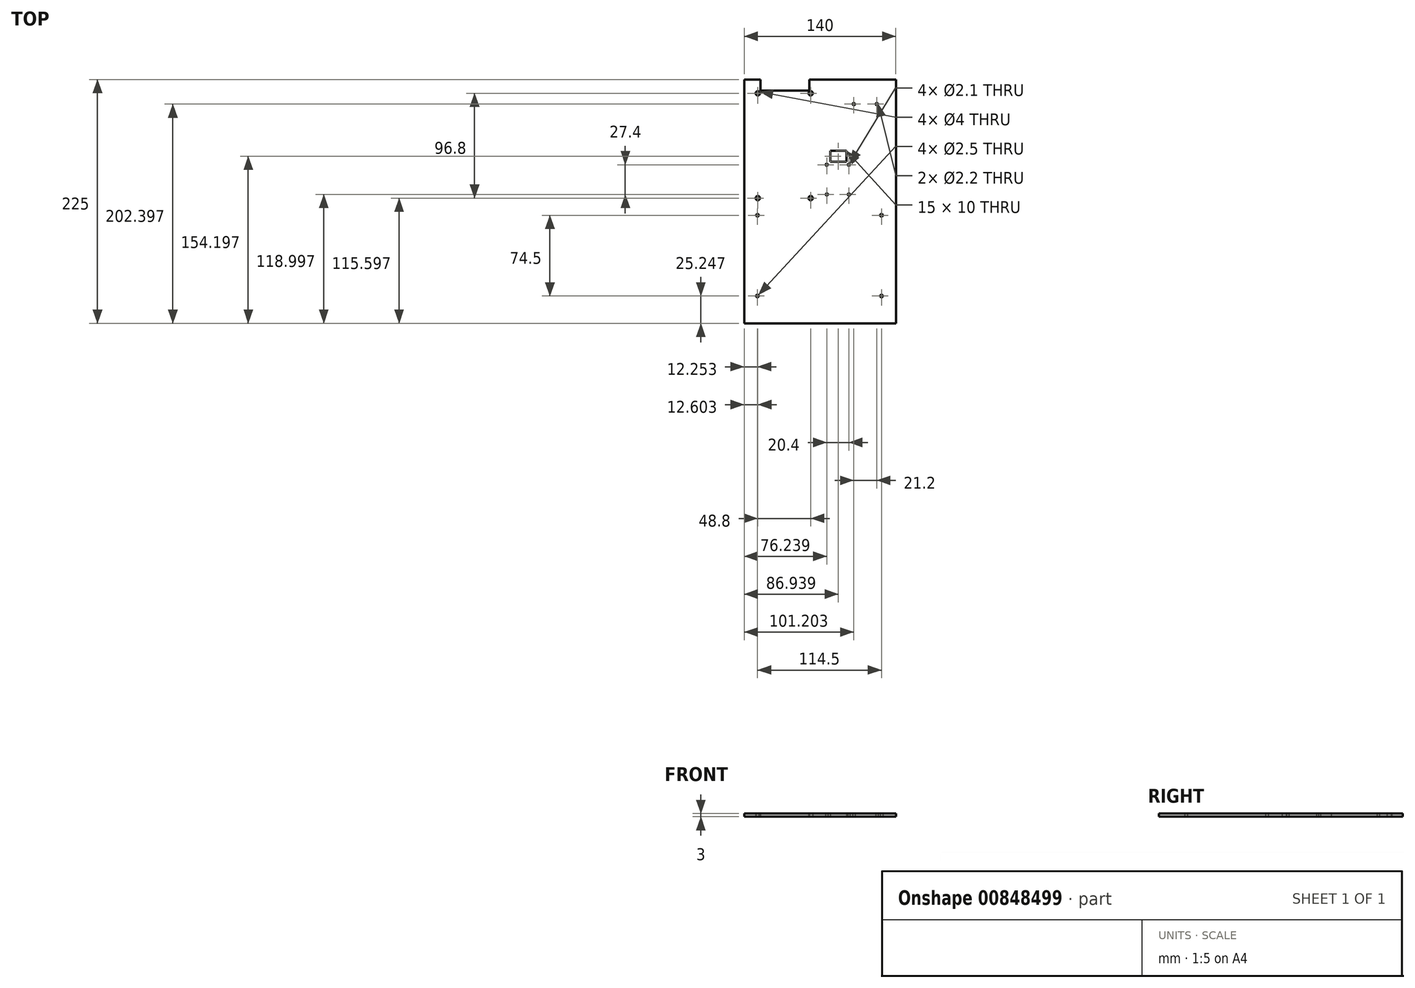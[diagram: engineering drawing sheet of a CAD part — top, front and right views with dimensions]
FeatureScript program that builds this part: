
annotation { "Feature Type Name" : "Feature", "Feature Type Description" : "" }
export const myFeature = defineFeature(function(context is Context, id is Id, definition is map)
    precondition{}
    {
        {
            var Q0;
            Q0=qCreatedBy(makeId("Top.planeOp"),FACE);
            var sketch = newSketch(context, id + "F0", { "sketchPlane" : qUnion([Q0])});
            skLineSegment(sketch, "E0.bottom", {"start": v(-96.6, 98.7) * mm, "end": v(43.4, 98.7) * mm});
            skLineSegment(sketch, "E0.top", {"start": v(-96.6, -126.3) * mm, "end": v(43.4, -126.3) * mm});
            skLineSegment(sketch, "E0.left", {"start": v(-96.6, 98.7) * mm, "end": v(-96.6, -126.3) * mm});
            skLineSegment(sketch, "E0.right", {"start": v(43.4, 98.7) * mm, "end": v(43.4, -126.3) * mm});
            skLineSegment(sketch, "E1.bottom", {"start": v(-86.6, 88.7) * mm, "end": v(-32.6, 88.7) * mm});
            skLineSegment(sketch, "E1.top", {"start": v(-86.6, -13.3) * mm, "end": v(-32.6, -13.3) * mm});
            skLineSegment(sketch, "E1.left", {"start": v(-86.6, 88.7) * mm, "end": v(-86.6, -13.3) * mm});
            skLineSegment(sketch, "E1.right", {"start": v(-32.6, 88.7) * mm, "end": v(-32.6, -13.3) * mm});
            skLineSegment(sketch, "E2.bottom", {"start": v(-87.6, -23.3) * mm, "end": v(33.4, -23.3) * mm});
            skLineSegment(sketch, "E2.top", {"start": v(-87.6, -104.3) * mm, "end": v(33.4, -104.3) * mm});
            skLineSegment(sketch, "E2.left", {"start": v(-87.6, -23.3) * mm, "end": v(-87.6, -104.3) * mm});
            skLineSegment(sketch, "E2.right", {"start": v(33.4, -23.3) * mm, "end": v(33.4, -104.3) * mm});
            skLineSegment(sketch, "E3.bottom", {"start": v(-23.16, 22.9) * mm, "end": v(2.84, 22.9) * mm});
            skLineSegment(sketch, "E3.top", {"start": v(-23.16, -10.1) * mm, "end": v(2.84, -10.1) * mm});
            skLineSegment(sketch, "E3.left", {"start": v(-23.16, 22.9) * mm, "end": v(-23.16, -10.1) * mm});
            skLineSegment(sketch, "E3.right", {"start": v(2.84, 22.9) * mm, "end": v(2.84, -10.1) * mm});
            skLineSegment(sketch, "E4.bottom", {"start": v(2, 78.7) * mm, "end": v(28.4, 78.7) * mm});
            skLineSegment(sketch, "E4.top", {"start": v(2, 42.9) * mm, "end": v(28.4, 42.9) * mm});
            skLineSegment(sketch, "E4.left", {"start": v(2, 78.7) * mm, "end": v(2, 42.9) * mm});
            skLineSegment(sketch, "E4.right", {"start": v(28.4, 78.7) * mm, "end": v(28.4, 42.9) * mm});
            skLineSegment(sketch, "E5", {"start": v(2.84, 22.9) * mm, "end": v(-2.16, 22.9) * mm});
            skLineSegment(sketch, "E6", {"start": v(-2.16, 22.9) * mm, "end": v(-17.16, 22.9) * mm});
            skLineSegment(sketch, "E7", {"start": v(-2.16, 22.9) * mm, "end": v(-2.16, 32.9) * mm});
            skLineSegment(sketch, "E8.bottom", {"start": v(-17.16, 22.9) * mm, "end": v(-2.16, 22.9) * mm});
            skLineSegment(sketch, "E8.top", {"start": v(-17.16, 32.9) * mm, "end": v(-2.16, 32.9) * mm});
            skLineSegment(sketch, "E8.left", {"start": v(-17.16, 22.9) * mm, "end": v(-17.16, 32.9) * mm});
            skLineSegment(sketch, "E9.bottom", {"start": v(-81.6, 98.7) * mm, "end": v(-36.6, 98.7) * mm});
            skLineSegment(sketch, "E9.top", {"start": v(-81.6, 88.7) * mm, "end": v(-36.6, 88.7) * mm});
            skLineSegment(sketch, "E9.left", {"start": v(-81.6, 98.7) * mm, "end": v(-81.6, 88.7) * mm});
            skLineSegment(sketch, "E9.right", {"start": v(-36.6, 98.7) * mm, "end": v(-36.6, 88.7) * mm});
            skLineSegment(sketch, "E10", {"start": v(33.4, -23.3) * mm, "end": v(33.4, -43.3) * mm});
            skLineSegment(sketch, "E11.bottom", {"start": v(33.4, -43.3) * mm, "end": v(43.4, -43.3) * mm});
            skLineSegment(sketch, "E11.top", {"start": v(33.4, -23.3) * mm, "end": v(43.4, -23.3) * mm});
            skLineSegment(sketch, "E11.left", {"start": v(33.4, -43.3) * mm, "end": v(33.4, -23.3) * mm});
            skLineSegment(sketch, "E11.right", {"start": v(43.4, -43.3) * mm, "end": v(43.4, -23.3) * mm});
            skCircle(sketch, "E12", {"center": v(-84.35, -101.04) * mm, "radius": 1.25 * mm});
            skCircle(sketch, "E13", {"center": v(-84.35, -26.54) * mm, "radius": 1.25 * mm});
            skCircle(sketch, "E14", {"center": v(30.15, -26.54) * mm, "radius": 1.25 * mm});
            skCircle(sketch, "E15", {"center": v(30.15, -101.04) * mm, "radius": 1.25 * mm});
            skCircle(sketch, "E16", {"center": v(4.6, 76.1) * mm, "radius": 1.1 * mm});
            skCircle(sketch, "E17", {"center": v(25.8, 76.1) * mm, "radius": 1.1 * mm});
            skCircle(sketch, "E18", {"center": v(0.04, 20.1) * mm, "radius": 1.05 * mm});
            skCircle(sketch, "E19", {"center": v(0.04, -7.3) * mm, "radius": 1.05 * mm});
            skCircle(sketch, "E20", {"center": v(-20.36, -7.3) * mm, "radius": 1.05 * mm});
            skCircle(sketch, "E21", {"center": v(-20.36, 20.1) * mm, "radius": 1.05 * mm});
            skLineSegment(sketch, "E22.bottom", {"start": v(-86.6, 88.7) * mm, "end": v(-84.4, 88.7) * mm});
            skLineSegment(sketch, "E22.left", {"start": v(-86.6, 88.7) * mm, "end": v(-86.6, 86.5) * mm});
            skLineSegment(sketch, "E23.bottom", {"start": v(-86.6, 88.7) * mm, "end": v(-84, 88.7) * mm});
            skLineSegment(sketch, "E23.left", {"start": v(-86.6, 88.7) * mm, "end": v(-86.6, 86.1) * mm});
            skCircle(sketch, "E24", {"center": v(-84, 86.1) * mm, "radius": 2 * mm});
            skLineSegment(sketch, "E25.bottom", {"start": v(-32.6, 88.7) * mm, "end": v(-35.2, 88.7) * mm});
            skLineSegment(sketch, "E25.left", {"start": v(-32.6, 88.7) * mm, "end": v(-32.6, 86.1) * mm});
            skCircle(sketch, "E26", {"center": v(-35.2, 86.1) * mm, "radius": 2 * mm});
            skLineSegment(sketch, "E27.bottom", {"start": v(-32.6, -13.3) * mm, "end": v(-35.2, -13.3) * mm});
            skLineSegment(sketch, "E27.left", {"start": v(-32.6, -13.3) * mm, "end": v(-32.6, -10.7) * mm});
            skLineSegment(sketch, "E28.bottom", {"start": v(-86.6, -13.3) * mm, "end": v(-84, -13.3) * mm});
            skLineSegment(sketch, "E28.left", {"start": v(-86.6, -13.3) * mm, "end": v(-86.6, -10.7) * mm});
            skCircle(sketch, "E29", {"center": v(-84, -10.7) * mm, "radius": 2 * mm});
            skCircle(sketch, "E30", {"center": v(-35.2, -10.7) * mm, "radius": 2 * mm});
            skSolve(sketch);
        }
        {
            var Q0;
            Q0=makeQuery(id+"F0.imprint","IMPRINT",FACE,{"disambiguationData":[TD([[makeQuery(id+"F0.imprint","IMPRINT",EDGE,{"derivedFrom":sQuery(id+"F0.wireOp",EDGE,"E2.bottom")}),-1.0]])]});
            var Q1;
            {var subQ1=sQuery(id+"F0.wireOp",EDGE,"E0.top");Q1=makeQuery(id+"F0.imprint","IMPRINT",FACE,{"disambiguationData":[TD([[makeQuery(id+"F0.imprint","IMPRINT",EDGE,{"derivedFrom":subQ1}),1.0]])]});}
            var Q2;
            Q2=makeQuery(id+"F0.imprint","IMPRINT",FACE,{"disambiguationData":[TD([[makeQuery(id+"F0.imprint","IMPRINT",EDGE,{"derivedFrom":sQuery(id+"F0.wireOp",EDGE,"E1.top")}),1.0]])]});
            var Q3;
            Q3=makeQuery(id+"F0.imprint","IMPRINT",FACE,{"disambiguationData":[TD([[makeQuery(id+"F0.imprint","IMPRINT",EDGE,{"derivedFrom":sQuery(id+"F0.wireOp",EDGE,"E3.bottom")}),-1.0]])]});
            var Q4;
            Q4=makeQuery(id+"F0.imprint","IMPRINT",FACE,{"disambiguationData":[TD([[makeQuery(id+"F0.imprint","IMPRINT",EDGE,{"derivedFrom":sQuery(id+"F0.wireOp",EDGE,"E8.bottom")}),1.0]])]});
            var Q5;
            Q5=makeQuery(id+"F0.imprint","IMPRINT",FACE,{"disambiguationData":[TD([[makeQuery(id+"F0.imprint","IMPRINT",EDGE,{"derivedFrom":sQuery(id+"F0.wireOp",EDGE,"E4.bottom")}),-1.0]])]});
            var Q6;
            Q6=makeQuery(id+"F0.imprint","IMPRINT",FACE,{"disambiguationData":[TD([[makeQuery(id+"F0.imprint","IMPRINT",EDGE,{"derivedFrom":sQuery(id+"F0.wireOp",EDGE,"E11.bottom")}),1.0]])]});
            var Q7;
            Q7=makeQuery(id+"F0.imprint","IMPRINT",FACE,{"disambiguationData":[TD([[makeQuery(id+"F0.imprint","IMPRINT",EDGE,{"derivedFrom":sQuery(id+"F0.wireOp",EDGE,"E9.bottom")}),-1.0]])]});
            extrude(context, id + "F1", {"entities" : qUnion([Q0, Q1, Q2, Q3, Q4, Q5, Q6, Q7]), "depth" : 3 * mm, "offsetDistance" : 25 * mm});
        }
    });
